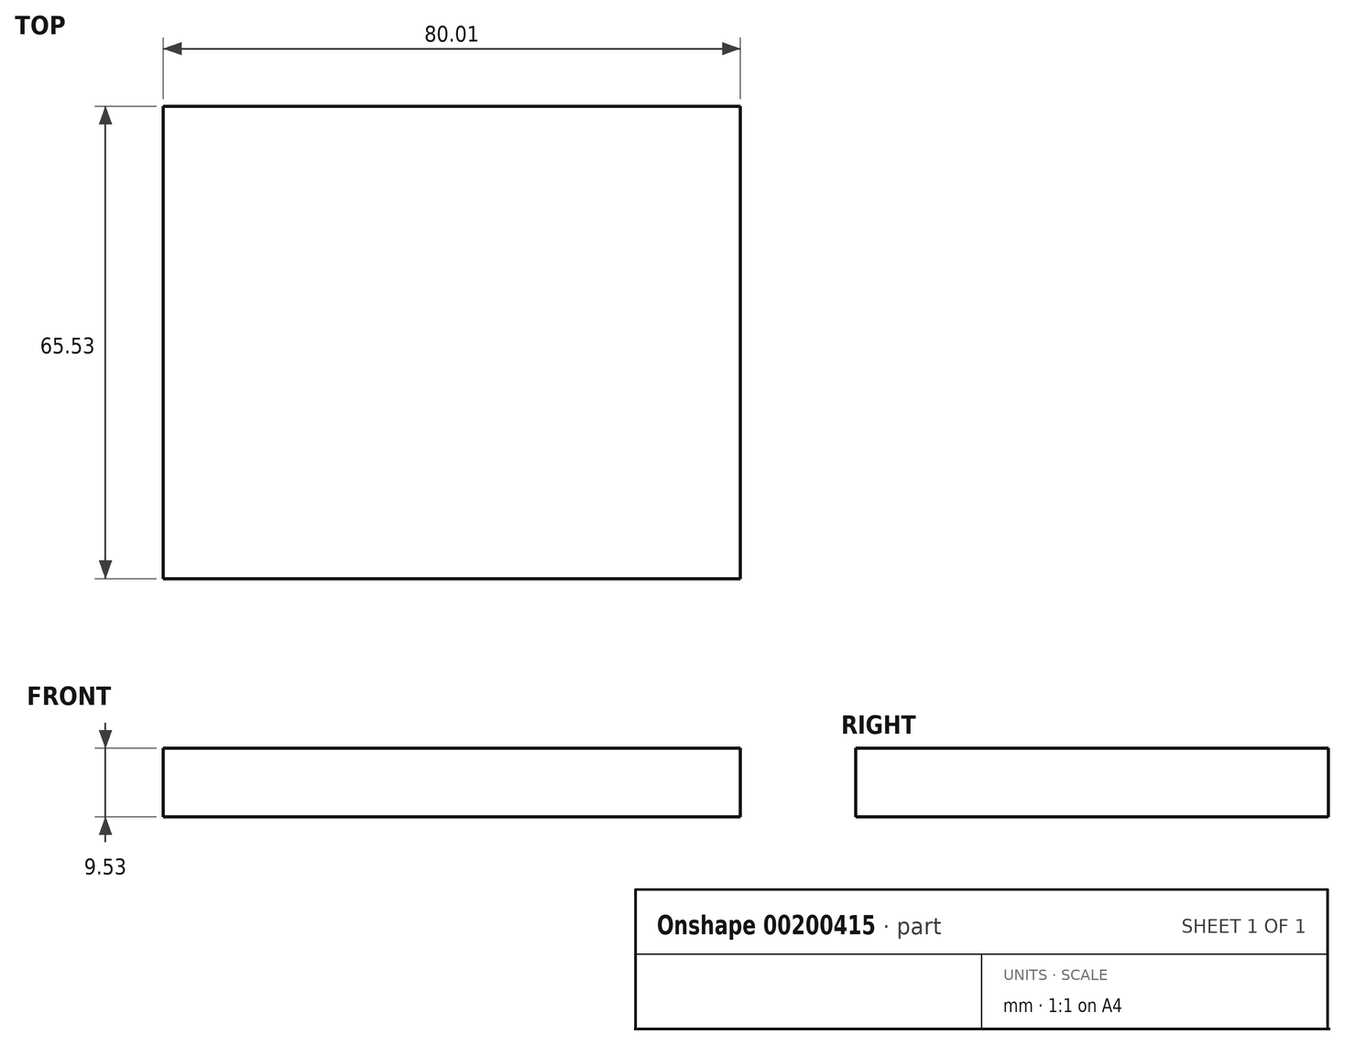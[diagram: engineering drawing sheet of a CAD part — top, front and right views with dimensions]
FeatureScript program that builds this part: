
annotation { "Feature Type Name" : "Feature", "Feature Type Description" : "" }
export const myFeature = defineFeature(function(context is Context, id is Id, definition is map)
    precondition{}
    {
        {
            var Q0;
            Q0=qCreatedBy(makeId("Top.planeOp"), FACE);
            var sketch = newSketch(context, id + "F0", { "sketchPlane" : qUnion([Q0])});
            skLineSegment(sketch, "E0.bottom", {"start": v(0, 0) * mm, "end": v(-80, 0) * mm});
            skLineSegment(sketch, "E0.top", {"start": v(0, -65.53) * mm, "end": v(-80, -65.53) * mm});
            skLineSegment(sketch, "E0.left", {"start": v(0, 0) * mm, "end": v(0, -65.53) * mm});
            skLineSegment(sketch, "E0.right", {"start": v(-80.01, 0) * mm, "end": v(-80, -65.53) * mm});
            skSolve(sketch);
        }
        {
            var Q0;
            Q0 = qSketchRegion(id + "F0", true);
            extrude(context, id + "F1", {"entities" : qUnion([Q0]), "depth" : 9.52 * mm, "offsetDistance" : 25.4 * mm});
        }
    });
